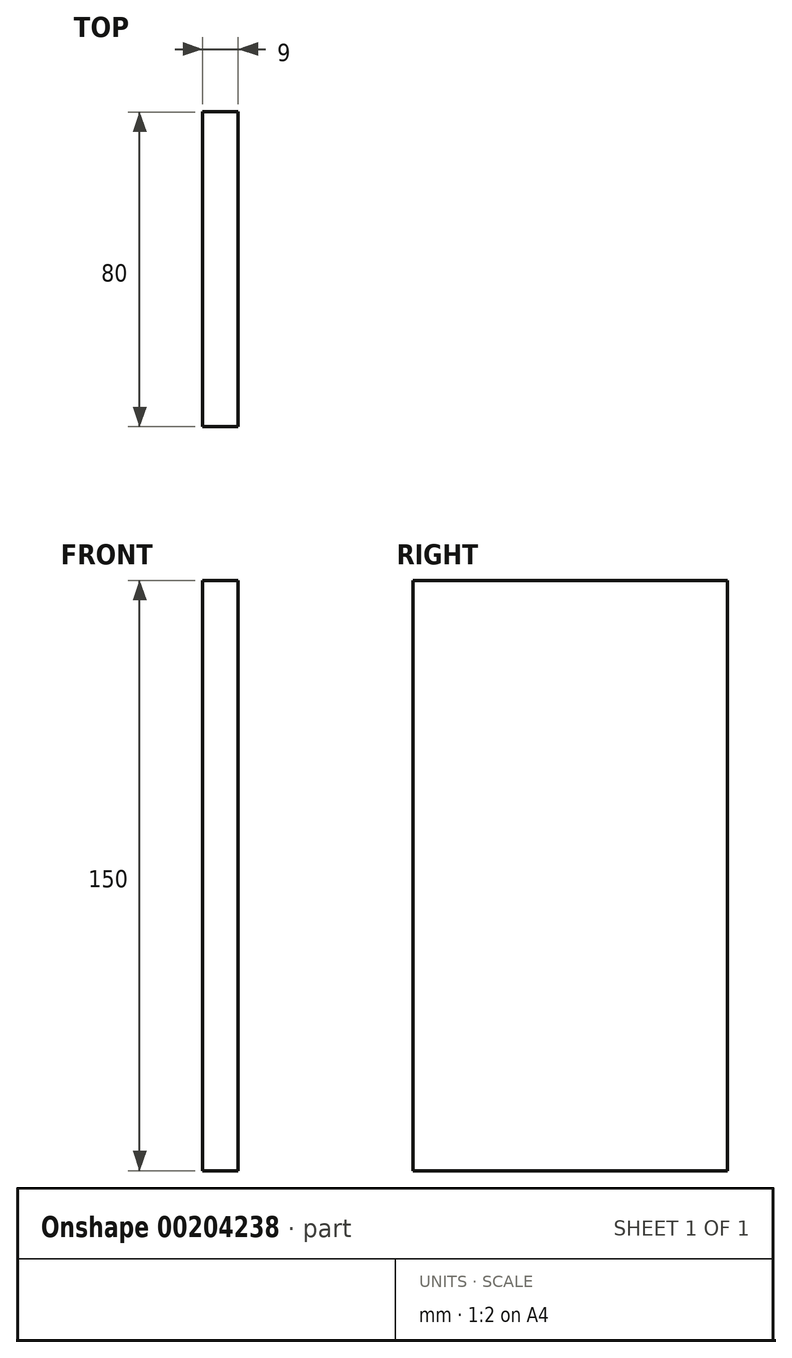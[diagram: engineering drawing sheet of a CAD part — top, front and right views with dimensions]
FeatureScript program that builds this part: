
annotation { "Feature Type Name" : "Feature", "Feature Type Description" : "" }
export const myFeature = defineFeature(function(context is Context, id is Id, definition is map)
    precondition{}
    {
        {
            var Q0;
            Q0=qCreatedBy(makeId("Right.planeOp"),FACE);
            var sketch = newSketch(context, id + "F0", { "sketchPlane" : qUnion([Q0])});
            skLineSegment(sketch, "E0.bottom", {"start": v(-51, 104.07) * mm, "end": v(29, 104.07) * mm});
            skLineSegment(sketch, "E0.top", {"start": v(-51, -45.93) * mm, "end": v(29, -45.93) * mm});
            skLineSegment(sketch, "E0.left", {"start": v(-51, 104.07) * mm, "end": v(-51, -45.93) * mm});
            skLineSegment(sketch, "E0.right", {"start": v(29, 104.07) * mm, "end": v(29, -45.93) * mm});
            skSolve(sketch);
        }
        {
            var Q0;
            Q0 = qSketchRegion(id + "F0", true);
            extrude(context, id + "F1", {"entities" : qUnion([Q0]), "depth" : 9 * mm});
        }
    });
